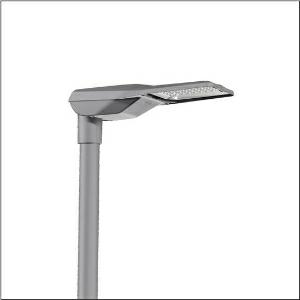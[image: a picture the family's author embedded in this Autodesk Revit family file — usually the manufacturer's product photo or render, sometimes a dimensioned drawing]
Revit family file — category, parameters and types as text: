
# Revit family: streetlight_sl_21_iq_mini___st1_5a_5xe2p41g08hb_3230
name_source: partatom
category: Lighting Fixtures
units: mm (PartAtom-declared; Revit-internal decimal feet)

## family parameters
Cut with Voids When Loaded = No
Host = Face
Light Source = No
Part Type = Normal
Room Calculation Point = No
Round Connector Dimension = Use Diameter
Shared = No

## types (1)
- --- (1 x LED, 9690 lm, 70.9 W, 4000K)
    Apparent Load = 71 VA
    CIE Flux Codes = 22 53 95 100 100
    Color Rendering = 70
    Color Temperature = 4000K
    Default Elevation = 1800 mm
    Description = Streetlight SL 21 iQ mini, mast luminaire, primary light control with lens, of PMMA, primary optical cover: cover, of toughened safety glass, transparent, light distribution: ST1.5a, light emission: direct distribution, primary light characteristic: asymmetric, installation type: post-top, side-entry, LED, High Power LED, rated luminous flux: 9.690lm, luminous efficacy: 137lm/W, light colour: 740, colour temperature: 4000K, control gear: iQ Street-Remote, control: Street-Remote, Auto-Match, Temp-Guard, Lumen-Switch, Night-Set, Smart-Wire, Light-Fading, Desk-Remote (wireless, voltage-free reading and setting of iQ features in the workshop via application-optimized NFC function/RFID function), optimised constant luminous flux control (CLO 2.0), pre-setting: linear dimming characteristic, mains connection: 220..240V, AC, 50/60Hz, start of lifetime: 71W, end of service life: 75W, reduction: 31W, luminaire housing, of diecast aluminium, powder-coated, SITECO metallic grey (DB 702S), corrosivity category C5 high according to DIN EN ISO 12944, please order mast flange separately, inclination adjustable: 0°, 5°, 10°, 15°, sealing non-destructively replaceable, multi-level sealing system, length: 628mm, width: 235mm, height: 110mm, mast flange for spigot size: 42mm (side-entry): 5XC10008XM4, 60/48mm (side-entry/post-top): 5XC10108XM2, 76/60mm (side-entry/post-top): 5XC10108XM1, mounting height: 4..8m, protection rating (complete): IP66, insulation class (complete): insulation class II (safety insulation), certification: CE, ENEC, ENEC+, VDE, impact resistance: IK10, permissible operating ambient temperature for outdoor applications: -40..+50°C, standard-compliant lighting for roads and squares, packaging unit: 1 piece

Light Distribution: ST1.5a
    Height = 110 mm
    Lamp = 1 x LED
    Lamp Light Flux = 9690 lm
    Lamp Power = 70.9 W
    Lamp count = 1
    Length = 625 mm
    Luminous efficacy = 137 lm/W
    Manufacturer = Siteco
    ModVariant = No
    Model = 5XE2P41G08HB
    Number of Poles = 1
    OnlyDefault = Yes
    Power Factor = 1
    Product Name = Streetlight SL 21 iQ mini | ST1.5a
    Product group = mast luminaire | pylon top
    ProductGroupID = 6100
    Protection Class = Protection class II
    Protection Degree = IP 66
    RLX_Detail_Level = 1
    RLX_Emergency_Light_Flux = 0 lm
    RLX_Emergency_Type = 0
    RLX_Emergency_Type_DB = No
    RlxData = <blob elided: 29901 chars, md5=57b343ee>
    Socket = socket
    Standby Power = 0 W
    System Light Flux = 9690 lm
    System Power = 71 W
    Type Comments = factory setting: luminous flux: 100 % | dim-lin: 254 | 711 mA
    Type Image = l_1003519.jpg
    URL = http://relux.com
    VarID = @adj_156463
    Voltage = 0 V
    Weight = 0.00 kg
    Width = 234 mm

## geometry (parser evidence)
native form markers: Blend x4, Sweep x9
no freeform markers — native parametric forms only
